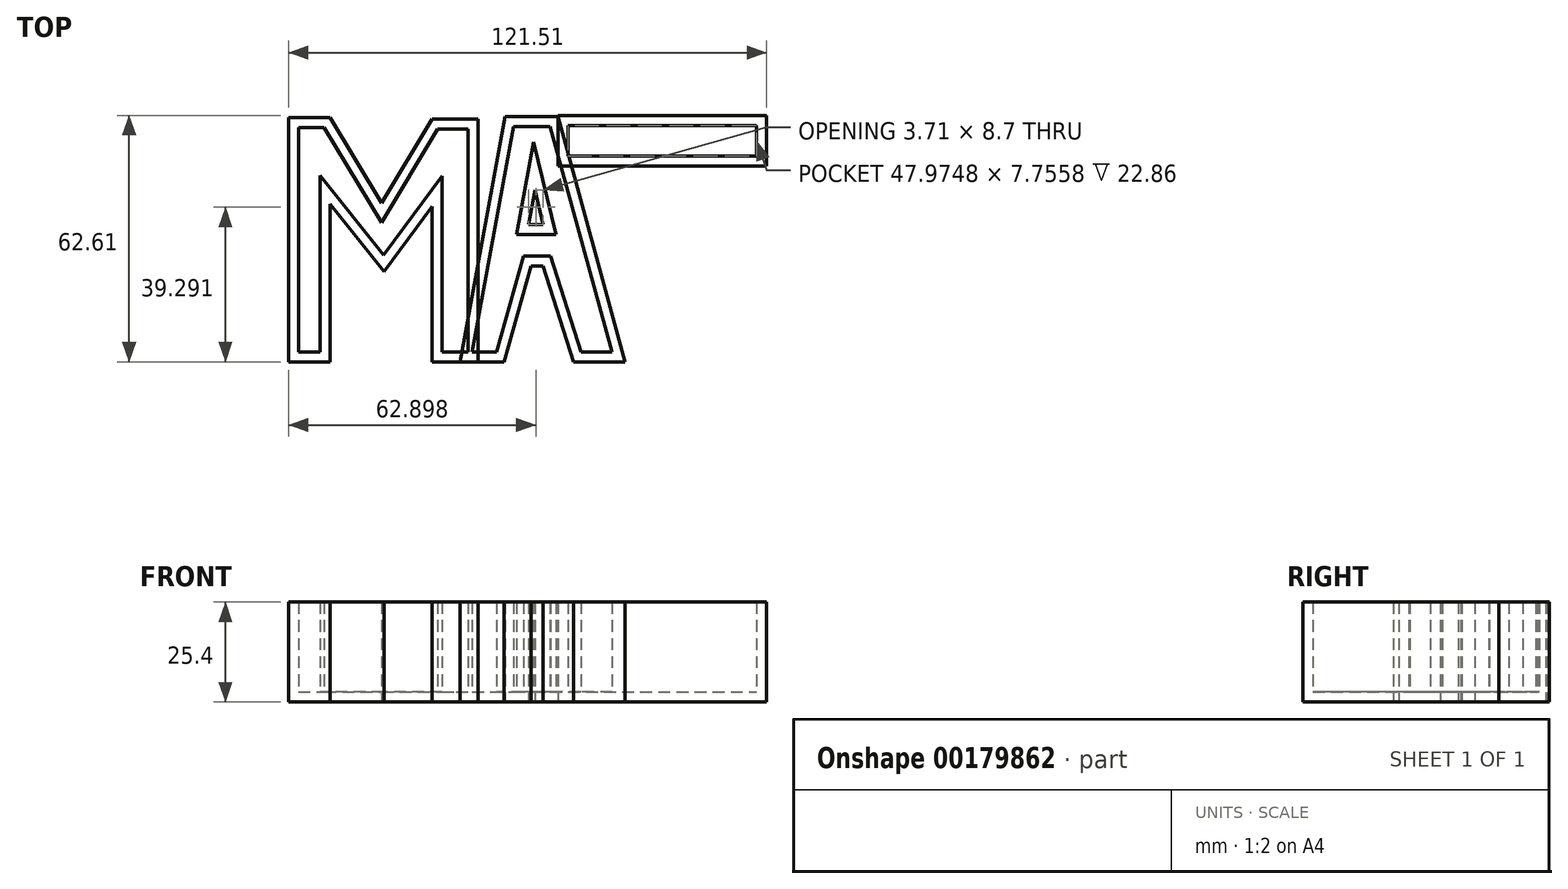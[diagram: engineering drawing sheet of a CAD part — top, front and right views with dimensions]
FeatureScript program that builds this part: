
annotation { "Feature Type Name" : "Feature", "Feature Type Description" : "" }
export const myFeature = defineFeature(function(context is Context, id is Id, definition is map)
    precondition{}
    {
        {
            var Q0;
            Q0=qCreatedBy(makeId("Top.planeOp"),FACE);
            var sketch = newSketch(context, id + "F0", { "sketchPlane" : qUnion([Q0])});
            skLineSegment(sketch, "E0.bottom", {"start": v(-68.46, 62.04) * mm, "end": v(-57.9, 62.04) * mm});
            skLineSegment(sketch, "E0.top", {"start": v(-68.46, 0) * mm, "end": v(-57.9, 0) * mm});
            skLineSegment(sketch, "E0.left", {"start": v(-68.46, 62.04) * mm, "end": v(-68.46, 0) * mm});
            skLineSegment(sketch, "E0.right", {"start": v(-57.9, 62.04) * mm, "end": v(-57.9, 0) * mm});
            skLineSegment(sketch, "E1.bottom", {"start": v(-31.95, 61.75) * mm, "end": v(-20.25, 61.75) * mm});
            skLineSegment(sketch, "E1.top", {"start": v(-31.95, 0) * mm, "end": v(-20.25, 0) * mm});
            skLineSegment(sketch, "E1.left", {"start": v(-31.95, 61.75) * mm, "end": v(-31.95, 0) * mm});
            skLineSegment(sketch, "E1.right", {"start": v(-20.25, 61.75) * mm, "end": v(-20.25, 0) * mm});
            skLineSegment(sketch, "E2", {"start": v(-57.9, 62.04) * mm, "end": v(-44.78, 40.36) * mm});
            skLineSegment(sketch, "E3", {"start": v(-44.78, 40.36) * mm, "end": v(-31.95, 61.75) * mm});
            skLineSegment(sketch, "E4", {"start": v(-31.95, 39.5) * mm, "end": v(-44.21, 22.96) * mm});
            skLineSegment(sketch, "E5", {"start": v(-44.21, 22.96) * mm, "end": v(-57.9, 40.08) * mm});
            skSolve(sketch);
        }
        {
            var Q0;
            Q0=qCreatedBy(makeId("Top.planeOp"),FACE);
            var sketch = newSketch(context, id + "F1", { "sketchPlane" : qUnion([Q0])});
            skLineSegment(sketch, "E6", {"start": v(-24.82, 0) * mm, "end": v(-13.4, 62.33) * mm});
            skLineSegment(sketch, "E7", {"start": v(-13.4, 62.33) * mm, "end": v(0, 62.33) * mm});
            skLineSegment(sketch, "E8", {"start": v(0, 62.33) * mm, "end": v(17.11, 0) * mm});
            skLineSegment(sketch, "E9", {"start": v(17.11, 0) * mm, "end": v(4, 0) * mm});
            skLineSegment(sketch, "E10", {"start": v(4, 0) * mm, "end": v(-3.7, 24.39) * mm});
            skLineSegment(sketch, "E11", {"start": v(-3.7, 24.39) * mm, "end": v(-6.85, 24.39) * mm});
            skLineSegment(sketch, "E12", {"start": v(-6.85, 24.39) * mm, "end": v(-13.7, 0) * mm});
            skLineSegment(sketch, "E13", {"start": v(-24.82, 0) * mm, "end": v(-13.7, 0) * mm});
            skLineSegment(sketch, "E14", {"start": v(-5.82, 43.64) * mm, "end": v(-7.42, 34.94) * mm});
            skLineSegment(sketch, "E15", {"start": v(-5.82, 43.64) * mm, "end": v(-3.7, 34.94) * mm});
            skLineSegment(sketch, "E16", {"start": v(-3.7, 34.94) * mm, "end": v(-7.42, 34.94) * mm});
            skSolve(sketch);
        }
        {
            var Q0;
            Q0=qCreatedBy(makeId("Top.planeOp"),FACE);
            var sketch = newSketch(context, id + "F2", { "sketchPlane" : qUnion([Q0])});
            skLineSegment(sketch, "E17.bottom", {"start": v(0, 62.61) * mm, "end": v(53.05, 62.61) * mm});
            skLineSegment(sketch, "E17.top", {"start": v(0, 49.77) * mm, "end": v(53.05, 49.77) * mm});
            skLineSegment(sketch, "E17.left", {"start": v(0, 62.61) * mm, "end": v(0, 49.77) * mm});
            skLineSegment(sketch, "E17.right", {"start": v(53.05, 62.61) * mm, "end": v(53.05, 49.77) * mm});
            skLineSegment(sketch, "E18.bottom", {"start": v(20.54, 49.77) * mm, "end": v(33.37, 49.77) * mm});
            skLineSegment(sketch, "E18.top", {"start": v(20.54, 0) * mm, "end": v(33.37, 0) * mm});
            skLineSegment(sketch, "E18.left", {"start": v(20.54, 49.77) * mm, "end": v(20.54, 0) * mm});
            skLineSegment(sketch, "E18.right", {"start": v(33.37, 49.77) * mm, "end": v(33.37, 0) * mm});
            skSolve(sketch);
        }
        {
            var Q0;
            {var subQ1=sQuery(id+"F0.wireOp",EDGE,"E2");Q0=makeQuery(id+"F0.imprint","IMPRINT",FACE,{"disambiguationData":[TD([[makeQuery(id+"F0.imprint","IMPRINT",EDGE,{"derivedFrom":subQ1}),-1.0]])]});}
            var Q1;
            {var subQ1=sQuery(id+"F0.wireOp",EDGE,"E0.bottom");Q1=makeQuery(id+"F0.imprint","IMPRINT",FACE,{"disambiguationData":[TD([[makeQuery(id+"F0.imprint","IMPRINT",EDGE,{"derivedFrom":subQ1}),-1.0]])]});}
            var Q2;
            {var subQ3=sQuery(id+"F0.wireOp",EDGE,"E1.bottom");Q2=makeQuery(id+"F0.imprint","IMPRINT",FACE,{"disambiguationData":[TD([[makeQuery(id+"F0.imprint","IMPRINT",EDGE,{"derivedFrom":subQ3}),-1.0]])]});}
            var Q3;
            Q3=makeQuery(id+"F1.imprint","IMPRINT",FACE,{"disambiguationData":[TD([[makeQuery(id+"F1.imprint","IMPRINT",EDGE,{"derivedFrom":sQuery(id+"F1.wireOp",EDGE,"E6")}),-1.0]])]});
            var Q4;
            Q4=makeQuery(id+"F2.imprint","IMPRINT",FACE,{"disambiguationData":[TD([[makeQuery(id+"F2.imprint","IMPRINT",EDGE,{"derivedFrom":sQuery(id+"F2.wireOp",EDGE,"E17.bottom")}),-1.0]])]});
            var Q5;
            Q5=makeQuery(id+"F2.imprint","IMPRINT",FACE,{"disambiguationData":[TD([[makeQuery(id+"F2.imprint","IMPRINT",EDGE,{"derivedFrom":sQuery(id+"F2.wireOp",EDGE,"E18.bottom")}),-1.0]])]});
            extrude(context, id + "F3", {"entities" : qUnion([Q0, Q1, Q2, Q3, Q4, Q5]), "depth" : 25.4 * mm});
        }
        {
            var Q0;
            Q0=makeQuery(id+"F3.opExtrude","CAP_FACE",FACE,{"disambiguationData":[OSD([sQuery(id+"F0.wireOp",EDGE,"E0.bottom"),sQuery(id+"F0.wireOp",EDGE,"E0.top"),sQuery(id+"F0.wireOp",EDGE,"E0.left"),sQuery(id+"F0.wireOp",EDGE,"E0.right"),sQuery(id+"F0.wireOp",EDGE,"E1.bottom"),sQuery(id+"F0.wireOp",EDGE,"E1.top"),sQuery(id+"F0.wireOp",EDGE,"E1.left"),sQuery(id+"F0.wireOp",EDGE,"E1.right"),sQuery(id+"F0.wireOp",EDGE,"E2"),sQuery(id+"F0.wireOp",EDGE,"E3"),sQuery(id+"F0.wireOp",EDGE,"E4"),sQuery(id+"F0.wireOp",EDGE,"E5")])],"isStart":false});
            var Q1;
            Q1=makeQuery(id+"F3.opExtrude","CAP_FACE",FACE,{"disambiguationData":[OSD([sQuery(id+"F1.wireOp",EDGE,"E6"),sQuery(id+"F1.wireOp",EDGE,"E7"),sQuery(id+"F1.wireOp",EDGE,"E8"),sQuery(id+"F1.wireOp",EDGE,"E9"),sQuery(id+"F1.wireOp",EDGE,"E10"),sQuery(id+"F1.wireOp",EDGE,"E11"),sQuery(id+"F1.wireOp",EDGE,"E12"),sQuery(id+"F1.wireOp",EDGE,"E13"),sQuery(id+"F1.wireOp",EDGE,"E14"),sQuery(id+"F1.wireOp",EDGE,"E15"),sQuery(id+"F1.wireOp",EDGE,"E16")])],"isStart":false});
            var Q2;
            Q2=makeQuery(id+"F3.opExtrude","CAP_FACE",FACE,{"disambiguationData":[OSD([sQuery(id+"F2.wireOp",EDGE,"E17.bottom"),sQuery(id+"F2.wireOp",EDGE,"E17.top"),sQuery(id+"F2.wireOp",EDGE,"E17.left"),sQuery(id+"F2.wireOp",EDGE,"E17.right"),sQuery(id+"F2.wireOp",EDGE,"E18.top"),sQuery(id+"F2.wireOp",EDGE,"E18.left"),sQuery(id+"F2.wireOp",EDGE,"E18.right")])],"isStart":false});
            shell(context, id + "F4", {"entities" : qUnion([Q0, Q1, Q2]), "thickness" : 2.54 * mm});
        }
    });
